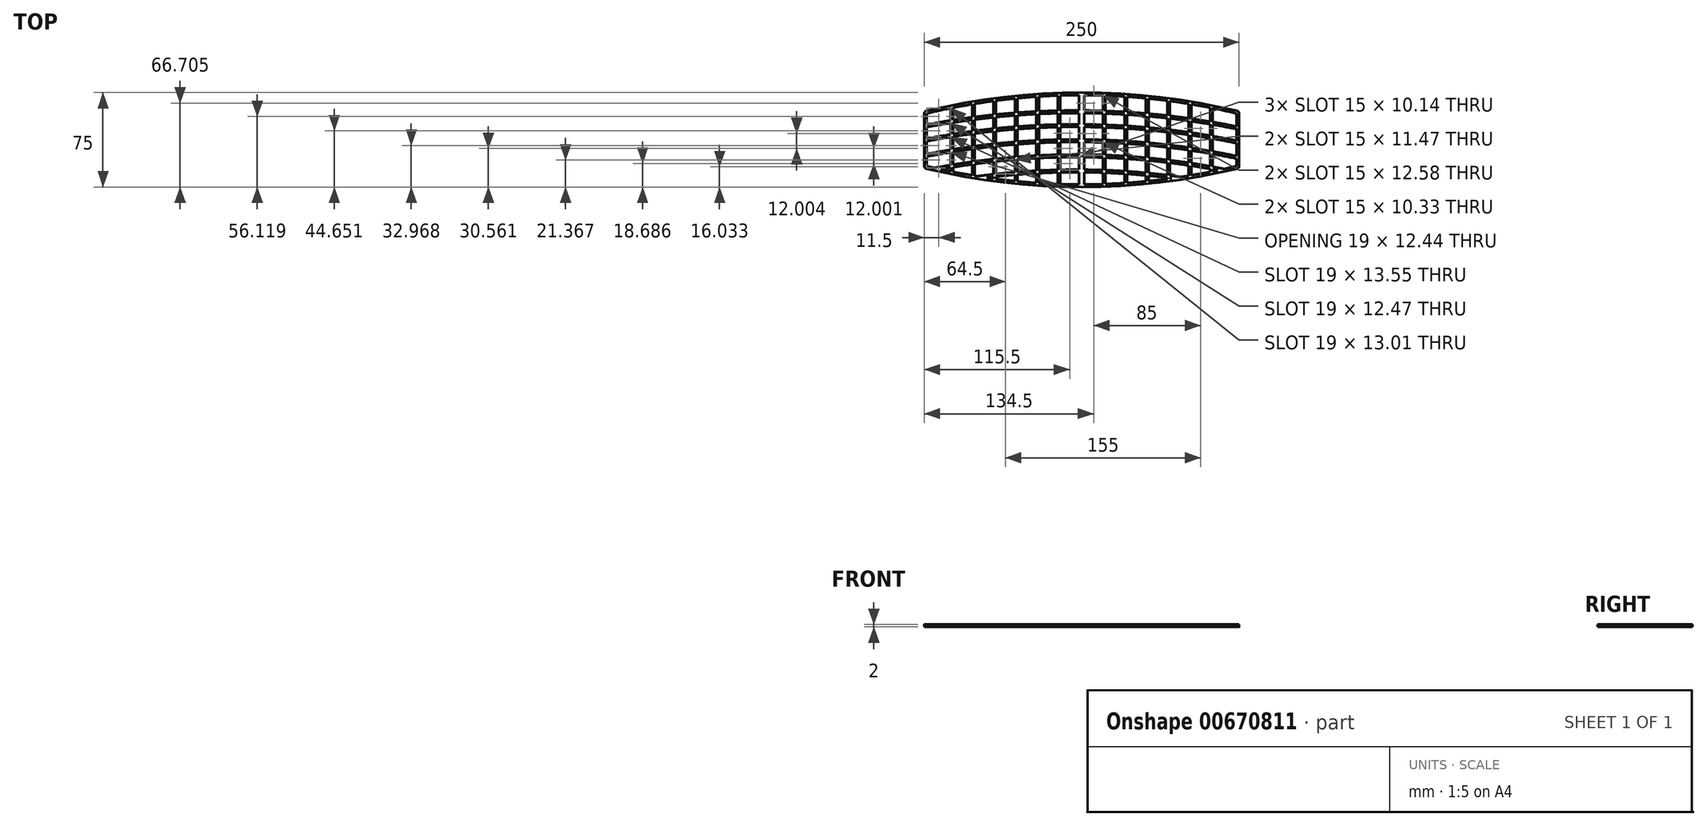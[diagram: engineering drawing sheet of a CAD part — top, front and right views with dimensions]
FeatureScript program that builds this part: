
annotation { "Feature Type Name" : "Feature", "Feature Type Description" : "" }
export const myFeature = defineFeature(function(context is Context, id is Id, definition is map)
    precondition{}
    {
        {
            var Q0;
            Q0=qCreatedBy(makeId("Top.planeOp"),FACE);
            var sketch = newSketch(context, id + "F0", { "sketchPlane" : qUnion([Q0])});
            skLineSegment(sketch, "E0.left", {"start": v(-125, 22.5) * mm, "end": v(-125, -22.5) * mm});
            skLineSegment(sketch, "E0.right", {"start": v(125, 22.5) * mm, "end": v(125, -22.5) * mm});
            skPoint(sketch, "E0.middle", {"position": v(0, 0) * mm});
            skLineSegment(sketch, "E1", {"start": v(-125, 22.5) * mm, "end": v(125, 22.5) * mm, "construction": true});
            skArc(sketch, "E2", {"start": v(125, 22.5) * mm, "mid": v(0, 37.5) * mm, "end": v(-125, 22.5) * mm});
            skLineSegment(sketch, "E3", {"start": v(-125, -22.5) * mm, "end": v(125, -22.5) * mm, "construction": true});
            skPoint(sketch, "E3.endSnap0", {"position": v(125, 0) * mm});
            skArc(sketch, "E4", {"start": v(-125, -22.5) * mm, "mid": v(0, -37.5) * mm, "end": v(125, -22.5) * mm});
            skPoint(sketch, "E5.orphan", {"position": v(-125, 37.5) * mm});
            skPoint(sketch, "E6.orphan", {"position": v(-125, -37.5) * mm});
            skPoint(sketch, "E0.bottom.end.orphan", {"position": v(125, 37.5) * mm});
            skPoint(sketch, "E0.top.end.orphan", {"position": v(125, -37.5) * mm});
            skSolve(sketch);
        }
        {
            var Q0;
            Q0 = qSketchRegion(id + "F0", true);
            extrude(context, id + "F1", {"entities" : qUnion([Q0]), "depth" : 2 * mm, "offsetDistance" : 25 * mm});
        }
        {
            var Q0;
            Q0=makeQuery(id+"F1.opExtrude","SWEPT_EDGE",EDGE,{"disambiguationData":[OSD([sQuery(id+"F0.wireOp",EDGE,"E0.left"),sQuery(id+"F0.wireOp",EDGE,"E4")])]});
            var Q1;
            Q1=makeQuery(id+"F1.opExtrude","SWEPT_EDGE",EDGE,{"disambiguationData":[OSD([sQuery(id+"F0.wireOp",EDGE,"E0.left"),sQuery(id+"F0.wireOp",EDGE,"E2")])]});
            var Q2;
            Q2=makeQuery(id+"F1.opExtrude","SWEPT_EDGE",EDGE,{"disambiguationData":[OSD([sQuery(id+"F0.wireOp",EDGE,"E0.right"),sQuery(id+"F0.wireOp",EDGE,"E2")])]});
            var Q3;
            Q3=makeQuery(id+"F1.opExtrude","SWEPT_EDGE",EDGE,{"disambiguationData":[OSD([sQuery(id+"F0.wireOp",EDGE,"E0.right"),sQuery(id+"F0.wireOp",EDGE,"E4")])]});
            fillet(context, id + "F2", {"entities" : qUnion([Q0, Q1, Q2, Q3]), "radius" : 2 * mm, "tangentPropagation" : true, "allowEdgeOverflow" : false});
        }
        {
            var Q0;
            Q0=makeQuery(id+"F1.opExtrude","CAP_FACE",FACE,{"disambiguationData":[OSD([sQuery(id+"F0.wireOp",EDGE,"E0.left"),sQuery(id+"F0.wireOp",EDGE,"E0.right"),sQuery(id+"F0.wireOp",EDGE,"E2"),sQuery(id+"F0.wireOp",EDGE,"E4")])],"isStart":false});
            var sketch = newSketch(context, id + "F3", { "sketchPlane" : qUnion([Q0])});
            skArc(sketch, "E7.0", {"start": v(123, 20.93) * mm, "mid": v(0, 35.5) * mm, "end": v(-123, 20.93) * mm});
            skLineSegment(sketch, "E7.1", {"start": v(123, 20.93) * mm, "end": v(123, -20.93) * mm});
            skArc(sketch, "E7.2", {"start": v(-123, -20.93) * mm, "mid": v(0, -35.5) * mm, "end": v(123, -20.93) * mm});
            skLineSegment(sketch, "E7.3", {"start": v(-123, 20.93) * mm, "end": v(-123, -20.93) * mm});
            skSolve(sketch);
        }
        {
            var Q0;
            Q0 = qSketchRegion(id + "F3", true);
            extrude(context, id + "F4", {"entities" : qUnion([Q0]), "operationType" : NewBodyOperationType.REMOVE, "oppositeDirection" : true, "depth" : 25 * mm, "offsetDistance" : 25 * mm});
        }
        {
            var Q0;
            Q0=makeQuery(id+"F3.imprint","IMPRINT",FACE,{"disambiguationData":[TD([[makeQuery(id+"F3.imprint","IMPRINT",EDGE,{"derivedFrom":sQuery(id+"F3.wireOp",EDGE,"E7.0")}),-1.0]])]});
            var sketch = newSketch(context, id + "F5", { "sketchPlane" : qUnion([Q0])});
            skArc(sketch, "E8", {"start": v(122.94, 8.52) * mm, "mid": v(0.02, 21.24) * mm, "end": v(-123.06, 10.07) * mm});
            skArc(sketch, "E9.0", {"start": v(123.34, 10.48) * mm, "mid": v(0.03, 23.24) * mm, "end": v(-123.43, 12.03) * mm});
            skLineSegment(sketch, "E10", {"start": v(122.94, 8.52) * mm, "end": v(123.34, 10.48) * mm});
            skLineSegment(sketch, "E11", {"start": v(-123.06, 10.07) * mm, "end": v(-123.43, 12.03) * mm});
            skSolve(sketch);
        }
        {
            var Q0;
            {var subQ5=sQuery(id+"F5.wireOp",EDGE,"E10");var subQ7=sQuery(id+"F5.wireOp",EDGE,"E8");var subQ8=makeQuery(id+"F5.imprint","INTERSECT",VERTEX,{"derivedFrom":[subQ7,subQ5]});Q0=makeQuery(id+"F5.imprint","IMPRINT",FACE,{"disambiguationData":[TD([[makeQuery(id+"F5.imprint","IMPRINT",EDGE,{"disambiguationData":[TD([[subQ8,-1.0]])],"derivedFrom":subQ7}),-1.0]])]});}
            var Q1;
            Q1=makeQuery(id+"F1.opExtrude","CAP_FACE",FACE,{"disambiguationData":[OSD([sQuery(id+"F0.wireOp",EDGE,"E0.left"),sQuery(id+"F0.wireOp",EDGE,"E0.right"),sQuery(id+"F0.wireOp",EDGE,"E2"),sQuery(id+"F0.wireOp",EDGE,"E4")])],"isStart":true});
            extrude(context, id + "F6", {"entities" : qUnion([Q0]), "operationType" : NewBodyOperationType.ADD, "endBound" : BoundingType.UP_TO_SURFACE, "oppositeDirection" : true, "depth" : 25 * mm, "endBoundEntityFace" : qUnion([Q1]), "offsetDistance" : 25 * mm});
        }
        {
            var Q0;
            Q0=makeQuery(id+"F3.imprint","IMPRINT",FACE,{"disambiguationData":[TD([[makeQuery(id+"F3.imprint","IMPRINT",EDGE,{"derivedFrom":sQuery(id+"F3.wireOp",EDGE,"E7.0")}),-1.0]])]});
            var sketch = newSketch(context, id + "F7", { "sketchPlane" : qUnion([Q0])});
            skArc(sketch, "E12.0", {"start": v(123.64, -0.8) * mm, "mid": v(0.08, 12.24) * mm, "end": v(-123.64, 0.8) * mm});
            skArc(sketch, "E13.0", {"start": v(123.24, -2.77) * mm, "mid": v(0.07, 10.24) * mm, "end": v(-123.26, -1.17) * mm});
            skLineSegment(sketch, "E14", {"start": v(-123.26, -1.17) * mm, "end": v(-123.64, 0.8) * mm});
            skLineSegment(sketch, "E15", {"start": v(123.24, -2.77) * mm, "end": v(123.64, -0.8) * mm});
            skArc(sketch, "E16.0", {"start": v(123.55, -13.05) * mm, "mid": v(0.14, 0.24) * mm, "end": v(-123.43, -11.4) * mm});
            skArc(sketch, "E17.0", {"start": v(123.54, -15.1) * mm, "mid": v(0.18, -1.76) * mm, "end": v(-123.35, -13.42) * mm});
            skArc(sketch, "E18.0", {"start": v(114.81, -23.5) * mm, "mid": v(-1.52, -11.75) * mm, "end": v(-117.94, -22.55) * mm});
            skArc(sketch, "E19.0", {"start": v(111.3, -24.85) * mm, "mid": v(-1.75, -13.75) * mm, "end": v(-114.89, -24) * mm});
            skLineSegment(sketch, "E20", {"start": v(111.3, -24.85) * mm, "end": v(114.81, -23.5) * mm});
            skLineSegment(sketch, "E21", {"start": v(123.54, -15.1) * mm, "end": v(123.55, -13.05) * mm});
            skLineSegment(sketch, "E22", {"start": v(-114.89, -24) * mm, "end": v(-117.94, -22.55) * mm});
            skLineSegment(sketch, "E23", {"start": v(-123.35, -13.42) * mm, "end": v(-123.43, -11.4) * mm});
            skArc(sketch, "E24.0", {"start": v(81.1, -29.87) * mm, "mid": v(-1.85, -23.75) * mm, "end": v(-84.84, -29.27) * mm});
            skArc(sketch, "E25.0", {"start": v(73.97, -30.9) * mm, "mid": v(-2.82, -25.74) * mm, "end": v(-79.62, -30.6) * mm});
            skLineSegment(sketch, "E26", {"start": v(73.97, -30.9) * mm, "end": v(81.1, -29.87) * mm});
            skLineSegment(sketch, "E27", {"start": v(-84.84, -29.27) * mm, "end": v(-79.62, -30.6) * mm});
            skSolve(sketch);
        }
        {
            var Q0;
            Q0 = qSketchRegion(id + "F7", true);
            var Q1;
            {var subQ0=sQuery(id+"F0.wireOp",EDGE,"E4");var subQ1=sQuery(id+"F0.wireOp",EDGE,"E2");var subQ2=sQuery(id+"F0.wireOp",EDGE,"E0.right");var subQ3=sQuery(id+"F0.wireOp",EDGE,"E0.left");Q1=makeQuery(id+"F6.boolean.opBoolean","MERGE",FACE,{"derivedFrom":[makeQuery(id+"F1.opExtrude","CAP_FACE",FACE,{"disambiguationData":[OSD([subQ3,subQ2,subQ1,subQ0])],"isStart":true}),makeQuery(id+"F6.opExtrude","CAP_FACE",FACE,{"disambiguationData":[OSD([subQ3,subQ2,subQ1,subQ0])],"isStart":false})]});}
            extrude(context, id + "F8", {"entities" : qUnion([Q0]), "operationType" : NewBodyOperationType.ADD, "endBound" : BoundingType.UP_TO_SURFACE, "oppositeDirection" : true, "depth" : 25 * mm, "endBoundEntityFace" : qUnion([Q1]), "offsetDistance" : 25 * mm});
        }
        {
            var Q0;
            Q0=makeQuery(id+"F3.imprint","IMPRINT",FACE,{"disambiguationData":[TD([[makeQuery(id+"F3.imprint","IMPRINT",EDGE,{"derivedFrom":sQuery(id+"F3.wireOp",EDGE,"E7.0")}),-1.0]])]});
            var sketch = newSketch(context, id + "F9", { "sketchPlane" : qUnion([Q0])});
            skLineSegment(sketch, "E28", {"start": v(0, 36.3) * mm, "end": v(0, -36.06) * mm});
            skLineSegment(sketch, "E29.0", {"start": v(-2, 36.3) * mm, "end": v(-2, -36.06) * mm});
            skLineSegment(sketch, "E30.0", {"start": v(-17, 36.3) * mm, "end": v(-17, -36.06) * mm});
            skLineSegment(sketch, "E31.0", {"start": v(-19, 36.3) * mm, "end": v(-19, -36.06) * mm});
            skLineSegment(sketch, "E32.0", {"start": v(-34, 35.46) * mm, "end": v(-34, -35.15) * mm});
            skLineSegment(sketch, "E33.0", {"start": v(-36, 35.23) * mm, "end": v(-36, -35.38) * mm});
            skLineSegment(sketch, "E34.0", {"start": v(-51, 34.41) * mm, "end": v(-51, -34.1) * mm});
            skLineSegment(sketch, "E35.0", {"start": v(-53, 33.83) * mm, "end": v(-53, -33.75) * mm});
            skLineSegment(sketch, "E36", {"start": v(-53, 33.83) * mm, "end": v(-51, 34.41) * mm});
            skLineSegment(sketch, "E37", {"start": v(-36, 35.23) * mm, "end": v(-34, 35.46) * mm});
            skLineSegment(sketch, "E38", {"start": v(-19, 36.3) * mm, "end": v(-17, 36.3) * mm});
            skLineSegment(sketch, "E39", {"start": v(-2, 36.3) * mm, "end": v(0, 36.3) * mm});
            skLineSegment(sketch, "E40", {"start": v(-53, -33.75) * mm, "end": v(-51, -34.1) * mm});
            skLineSegment(sketch, "E41", {"start": v(-36, -35.38) * mm, "end": v(-34, -35.15) * mm});
            skLineSegment(sketch, "E42", {"start": v(-19, -36.06) * mm, "end": v(-17, -36.06) * mm});
            skLineSegment(sketch, "E43", {"start": v(-2, -36.06) * mm, "end": v(0, -36.06) * mm});
            skLineSegment(sketch, "E44.0", {"start": v(-68, 32.06) * mm, "end": v(-68, -32) * mm});
            skLineSegment(sketch, "E45.0", {"start": v(-70, 31.5) * mm, "end": v(-70, -31.72) * mm});
            skLineSegment(sketch, "E46.0", {"start": v(-85, 29.7) * mm, "end": v(-85, -29.64) * mm});
            skLineSegment(sketch, "E47.0", {"start": v(-87, 29.7) * mm, "end": v(-87, -29.23) * mm});
            skLineSegment(sketch, "E48.0", {"start": v(-102, 26.53) * mm, "end": v(-102, -26.32) * mm});
            skLineSegment(sketch, "E49.0", {"start": v(-104, 25.83) * mm, "end": v(-104, -25.9) * mm});
            skLineSegment(sketch, "E50", {"start": v(-104, -25.9) * mm, "end": v(-102, -26.32) * mm});
            skLineSegment(sketch, "E51", {"start": v(-87, -29.23) * mm, "end": v(-85, -29.64) * mm});
            skLineSegment(sketch, "E52", {"start": v(-70, -31.72) * mm, "end": v(-68, -32) * mm});
            skLineSegment(sketch, "E53", {"start": v(-104, 25.83) * mm, "end": v(-102, 26.53) * mm});
            skLineSegment(sketch, "E54", {"start": v(-87, 29.7) * mm, "end": v(-85, 29.7) * mm});
            skLineSegment(sketch, "E55", {"start": v(-70, 31.5) * mm, "end": v(-68, 32.06) * mm});
            skLineSegment(sketch, "E56.MirrorCS", {"start": v(104, 25.83) * mm, "end": v(102, 26.53) * mm});
            skLineSegment(sketch, "E57.MirrorCS", {"start": v(53, 33.83) * mm, "end": v(51, 34.41) * mm});
            skLineSegment(sketch, "E58.MirrorCS", {"start": v(19, -36.06) * mm, "end": v(17, -36.06) * mm});
            skLineSegment(sketch, "E59.MirrorCS", {"start": v(104, -25.9) * mm, "end": v(102, -26.32) * mm});
            skLineSegment(sketch, "E60.MirrorCS", {"start": v(87, 29.7) * mm, "end": v(85, 29.7) * mm});
            skLineSegment(sketch, "E61.MirrorCS", {"start": v(87, -29.23) * mm, "end": v(85, -29.64) * mm});
            skLineSegment(sketch, "E62.MirrorCS", {"start": v(2, -36.06) * mm, "end": v(0, -36.06) * mm});
            skLineSegment(sketch, "E63.MirrorCS", {"start": v(70, 31.5) * mm, "end": v(68, 32.06) * mm});
            skLineSegment(sketch, "E64.MirrorCS", {"start": v(36, 35.23) * mm, "end": v(34, 35.46) * mm});
            skLineSegment(sketch, "E65.MirrorCS", {"start": v(53, -33.75) * mm, "end": v(51, -34.1) * mm});
            skLineSegment(sketch, "E66.MirrorCS", {"start": v(19, 36.3) * mm, "end": v(17, 36.3) * mm});
            skLineSegment(sketch, "E67.MirrorCS", {"start": v(36, -35.38) * mm, "end": v(34, -35.15) * mm});
            skLineSegment(sketch, "E68.MirrorCS", {"start": v(2, 36.3) * mm, "end": v(0, 36.3) * mm});
            skLineSegment(sketch, "E69.MirrorCS", {"start": v(70, -31.72) * mm, "end": v(68, -32) * mm});
            skLineSegment(sketch, "E70.MirrorCS", {"start": v(17, 36.3) * mm, "end": v(17, -36.06) * mm});
            skLineSegment(sketch, "E71.MirrorCS", {"start": v(70, 31.5) * mm, "end": v(70, -31.72) * mm});
            skLineSegment(sketch, "E72.MirrorCS", {"start": v(34, 35.46) * mm, "end": v(34, -35.15) * mm});
            skLineSegment(sketch, "E73.MirrorCS", {"start": v(87, 29.7) * mm, "end": v(87, -29.23) * mm});
            skLineSegment(sketch, "E74.MirrorCS", {"start": v(19, 36.3) * mm, "end": v(19, -36.06) * mm});
            skLineSegment(sketch, "E75.MirrorCS", {"start": v(85, 29.7) * mm, "end": v(85, -29.64) * mm});
            skLineSegment(sketch, "E76.MirrorCS", {"start": v(36, 35.23) * mm, "end": v(36, -35.38) * mm});
            skLineSegment(sketch, "E77.MirrorCS", {"start": v(51, 34.41) * mm, "end": v(51, -34.1) * mm});
            skLineSegment(sketch, "E78.MirrorCS", {"start": v(102, 26.53) * mm, "end": v(102, -26.32) * mm});
            skLineSegment(sketch, "E79.MirrorCS", {"start": v(53, 33.83) * mm, "end": v(53, -33.75) * mm});
            skLineSegment(sketch, "E80.MirrorCS", {"start": v(104, 25.83) * mm, "end": v(104, -25.9) * mm});
            skLineSegment(sketch, "E81.MirrorCS", {"start": v(2, 36.3) * mm, "end": v(2, -36.06) * mm});
            skLineSegment(sketch, "E82.MirrorCS", {"start": v(68, 32.06) * mm, "end": v(68, -32) * mm});
            skSolve(sketch);
        }
        {
            var Q0;
            Q0 = qSketchRegion(id + "F9", true);
            var Q1;
            {var subQ0=sQuery(id+"F0.wireOp",EDGE,"E4");var subQ1=sQuery(id+"F0.wireOp",EDGE,"E2");var subQ2=sQuery(id+"F0.wireOp",EDGE,"E0.right");var subQ3=sQuery(id+"F0.wireOp",EDGE,"E0.left");Q1=makeQuery(id+"F8.boolean.opBoolean","MERGE",FACE,{"derivedFrom":[makeQuery(id+"F6.boolean.opBoolean","MERGE",FACE,{"derivedFrom":[makeQuery(id+"F1.opExtrude","CAP_FACE",FACE,{"disambiguationData":[OSD([subQ3,subQ2,subQ1,subQ0])],"isStart":true}),makeQuery(id+"F6.opExtrude","CAP_FACE",FACE,{"disambiguationData":[OSD([subQ3,subQ2,subQ1,subQ0])],"isStart":false})]}),makeQuery(id+"F8.opExtrude","CAP_FACE",FACE,{"disambiguationData":[OSD([subQ3,subQ2,subQ1,subQ0]),OD(0.0)],"isStart":false}),makeQuery(id+"F8.opExtrude","CAP_FACE",FACE,{"disambiguationData":[OSD([subQ3,subQ2,subQ1,subQ0]),OD(1.0)],"isStart":false}),makeQuery(id+"F8.opExtrude","CAP_FACE",FACE,{"disambiguationData":[OSD([subQ3,subQ2,subQ1,subQ0]),OD(2.0)],"isStart":false}),makeQuery(id+"F8.opExtrude","CAP_FACE",FACE,{"disambiguationData":[OSD([subQ3,subQ2,subQ1,subQ0]),OD(3.0)],"isStart":false})]});}
            extrude(context, id + "F10", {"entities" : qUnion([Q0]), "operationType" : NewBodyOperationType.ADD, "endBound" : BoundingType.UP_TO_SURFACE, "oppositeDirection" : true, "depth" : 25 * mm, "endBoundEntityFace" : qUnion([Q1]), "offsetDistance" : 25 * mm});
        }
    });
